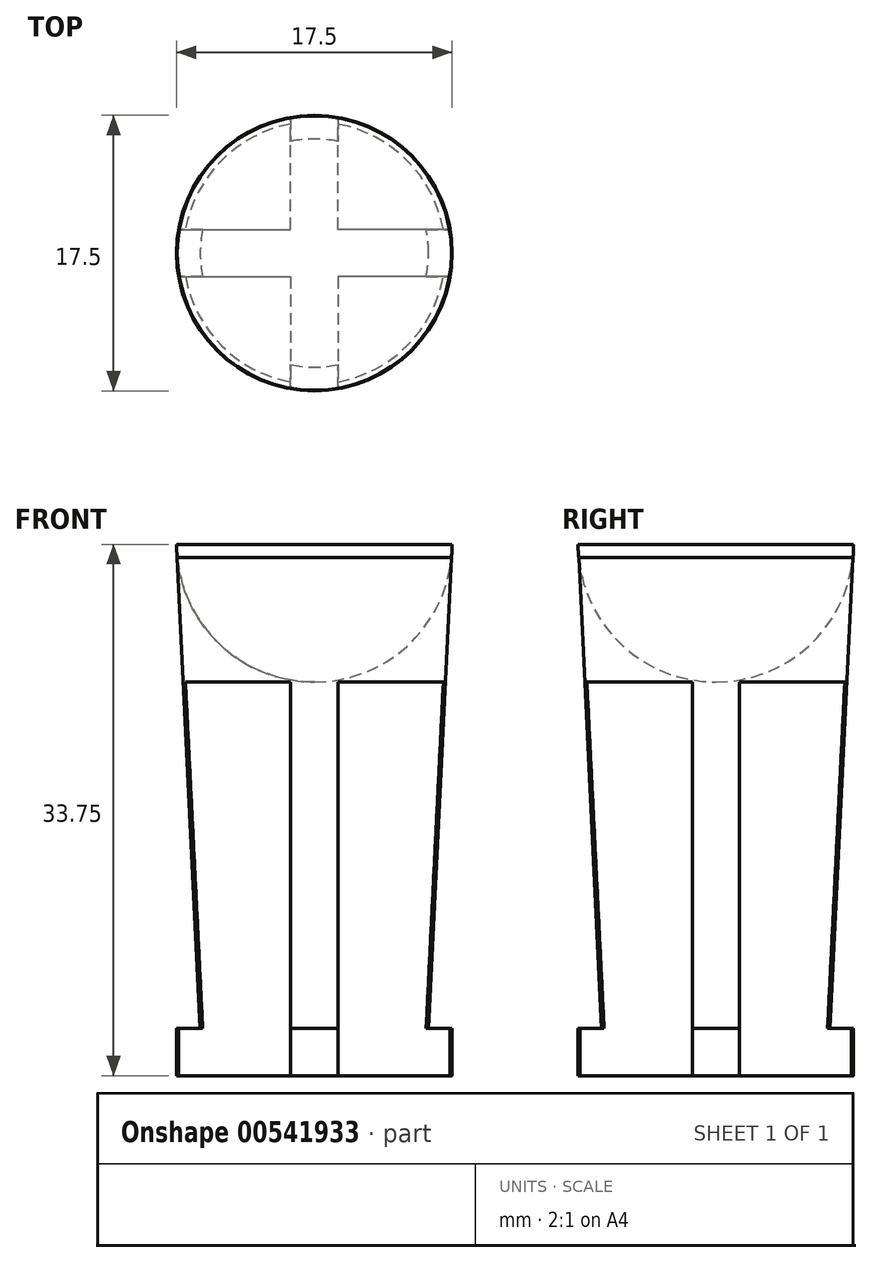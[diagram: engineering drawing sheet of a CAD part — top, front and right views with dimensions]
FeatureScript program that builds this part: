
annotation { "Feature Type Name" : "Feature", "Feature Type Description" : "" }
export const myFeature = defineFeature(function(context is Context, id is Id, definition is map)
    precondition{}
    {
        {
            var Q0;
            Q0=qCreatedBy(makeId("Front.planeOp"),FACE);
            var sketch = newSketch(context, id + "F0", { "sketchPlane" : qUnion([Q0])});
            skArc(sketch, "E0", {"start": v(-8.75, 0) * mm, "mid": v(-6.19, -6.19) * mm, "end": v(0, -8.75) * mm});
            skLineSegment(sketch, "E1", {"start": v(0, -8.75) * mm, "end": v(0, -30.75) * mm});
            skLineSegment(sketch, "E2", {"start": v(0, 0) * mm, "end": v(0, -33.75) * mm});
            skPoint(sketch, "E3.end.orphan", {"position": v(5.27, -8.75) * mm});
            skLineSegment(sketch, "E4", {"start": v(0, -30.75) * mm, "end": v(-8.75, -30.75) * mm});
            skLineSegment(sketch, "E5", {"start": v(-8.75, -30.75) * mm, "end": v(-8.75, -33.75) * mm});
            skLineSegment(sketch, "E6", {"start": v(-8.75, -33.75) * mm, "end": v(0, -33.75) * mm});
            skLineSegment(sketch, "E7", {"start": v(-8.75, 0) * mm, "end": v(-8.75, 10) * mm});
            skLineSegment(sketch, "E8", {"start": v(-8.75, 0) * mm, "end": v(-7.25, -30.75) * mm});
            skSolve(sketch);
        }
        {
            var Q0;
            Q0 = qSketchRegion(id + "F0", true);
            var Q1;
            Q1=sQuery(id+"F0.wireOp",EDGE,"E2");
            revolve(context, id + "F1", {"entities" : qUnion([Q0]), "axis" : qUnion([Q1]), "revolveType" : RevolveType.FULL});
        }
        {
            var Q0;
            Q0=makeQuery(id+"F1.opRevolve","SWEPT_FACE",FACE,{"disambiguationData":[OSD([sQuery(id+"F0.wireOp",EDGE,"E6")])]});
            var sketch = newSketch(context, id + "F2", { "sketchPlane" : qUnion([Q0])});
            skLineSegment(sketch, "E9", {"start": v(-8.62, 1.5) * mm, "end": v(-1.5, 1.5) * mm});
            skLineSegment(sketch, "E10.MirrorCS", {"start": v(8.62, 1.5) * mm, "end": v(1.5, 1.5) * mm});
            skLineSegment(sketch, "E11.MirrorCS", {"start": v(8.62, -1.5) * mm, "end": v(1.5, -1.5) * mm});
            skLineSegment(sketch, "E12.MirrorCS", {"start": v(-8.62, -1.5) * mm, "end": v(-1.5, -1.5) * mm});
            skLineSegment(sketch, "E13", {"start": v(-1.5, 1.5) * mm, "end": v(-1.5, 8.62) * mm});
            skLineSegment(sketch, "E14", {"start": v(-1.5, -1.5) * mm, "end": v(-1.5, -8.62) * mm});
            skLineSegment(sketch, "E15.MirrorCS", {"start": v(1.5, 1.5) * mm, "end": v(1.5, 8.62) * mm});
            skLineSegment(sketch, "E16.MirrorCS", {"start": v(1.5, -1.5) * mm, "end": v(1.5, -8.62) * mm});
            skArc(sketch, "E17", {"start": v(-1.5, 8.62) * mm, "mid": v(-6.28, 6.28) * mm, "end": v(-8.62, 1.5) * mm});
            skArc(sketch, "E18", {"start": v(8.62, 1.5) * mm, "mid": v(6.25, 6.25) * mm, "end": v(1.5, 8.62) * mm});
            skArc(sketch, "E19", {"start": v(1.5, -8.62) * mm, "mid": v(6.28, -6.28) * mm, "end": v(8.62, -1.5) * mm});
            skArc(sketch, "E20", {"start": v(-8.62, -1.5) * mm, "mid": v(-6.24, -6.24) * mm, "end": v(-1.5, -8.62) * mm});
            skSolve(sketch);
        }
        {
            var Q0;
            Q0 = qSketchRegion(id + "F2", true);
            extrude(context, id + "F3", {"entities" : qUnion([Q0]), "operationType" : NewBodyOperationType.REMOVE, "oppositeDirection" : true, "depth" : 25 * mm, "offsetDistance" : 25 * mm});
        }
    });
